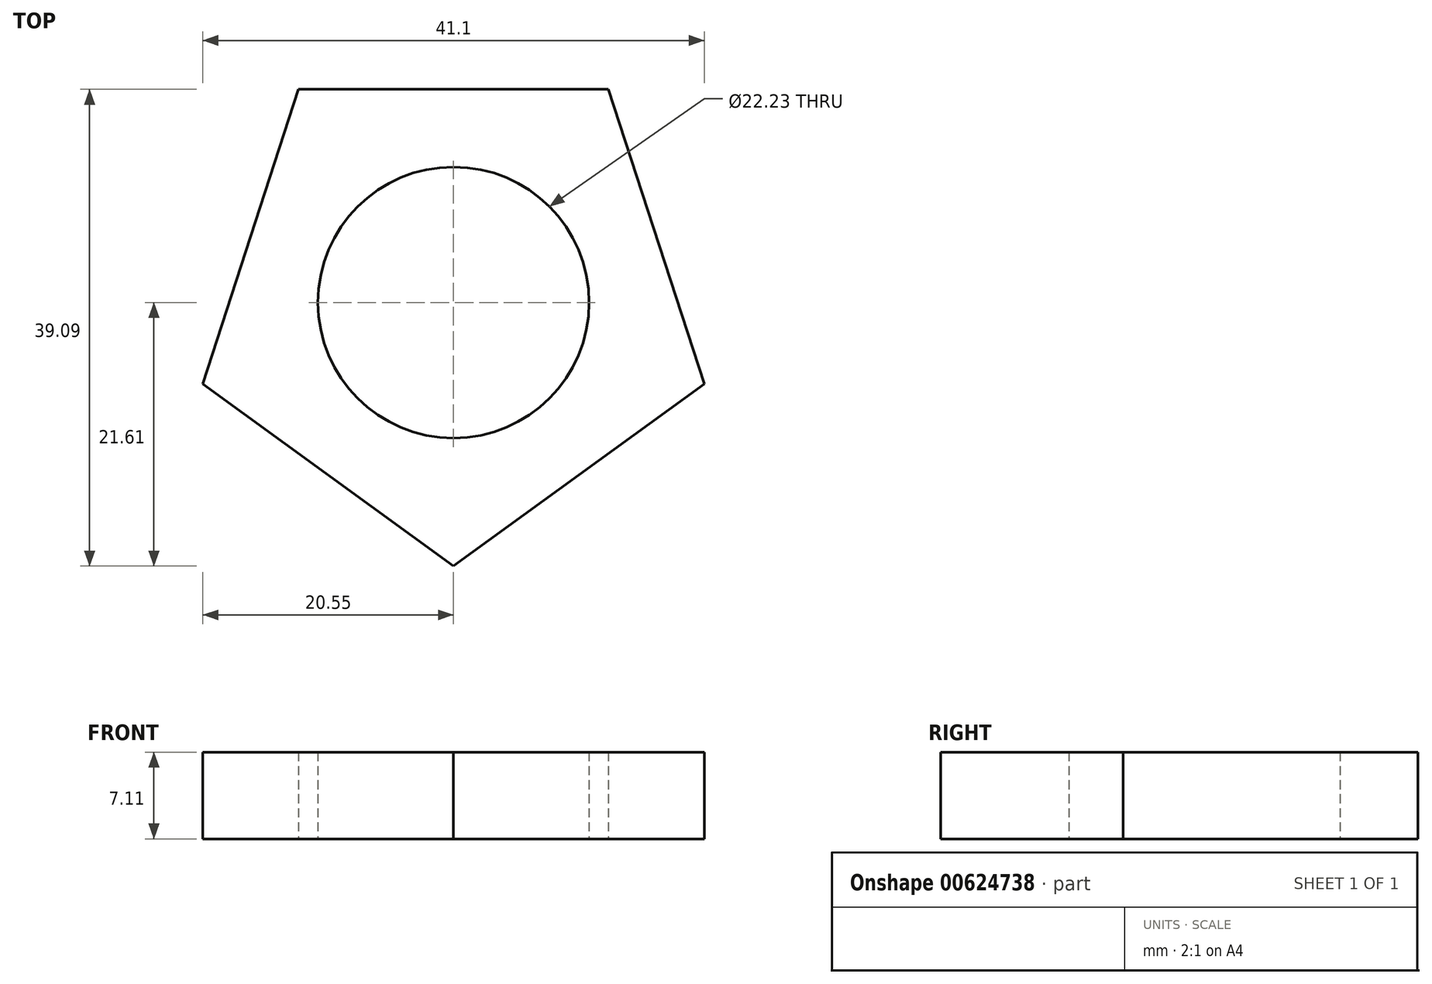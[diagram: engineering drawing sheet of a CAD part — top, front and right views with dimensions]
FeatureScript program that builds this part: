
annotation { "Feature Type Name" : "Feature", "Feature Type Description" : "" }
export const myFeature = defineFeature(function(context is Context, id is Id, definition is map)
    precondition{}
    {
        {
            var Q0;
            Q0=qCreatedBy(makeId("Top.planeOp"),FACE);
            var sketch = newSketch(context, id + "F0", { "sketchPlane" : qUnion([Q0])});
            skCircle(sketch, "E0.cCircle", {"center": v(0, 0) * mm, "radius": 17.48 * mm, "construction": true});
            skLineSegment(sketch, "E0.0", {"start": v(-12.7, 17.48) * mm, "end": v(12.7, 17.48) * mm});
            skLineSegment(sketch, "E0.1", {"start": v(12.7, 17.48) * mm, "end": v(20.55, -6.68) * mm});
            skLineSegment(sketch, "E0.2", {"start": v(20.55, -6.68) * mm, "end": v(0, -21.6) * mm});
            skLineSegment(sketch, "E0.3", {"start": v(0, -21.6) * mm, "end": v(-20.55, -6.68) * mm});
            skLineSegment(sketch, "E0.4", {"start": v(-20.55, -6.68) * mm, "end": v(-12.7, 17.48) * mm});
            skPoint(sketch, "E0.0.midPoint", {"position": v(0, 17.48) * mm});
            skCircle(sketch, "E1", {"center": v(0, 0) * mm, "radius": 11.11 * mm});
            skSolve(sketch);
        }
        {
            var Q0;
            Q0=makeQuery(id+"F0.imprint","IMPRINT",FACE,{"disambiguationData":[TD([[makeQuery(id+"F0.imprint","IMPRINT",EDGE,{"derivedFrom":sQuery(id+"F0.wireOp",EDGE,"E0.0")}),-1.0]])]});
            extrude(context, id + "F1", {"entities" : qUnion([Q0]), "depth" : 7.11 * mm, "offsetDistance" : 25.4 * mm});
        }
    });
